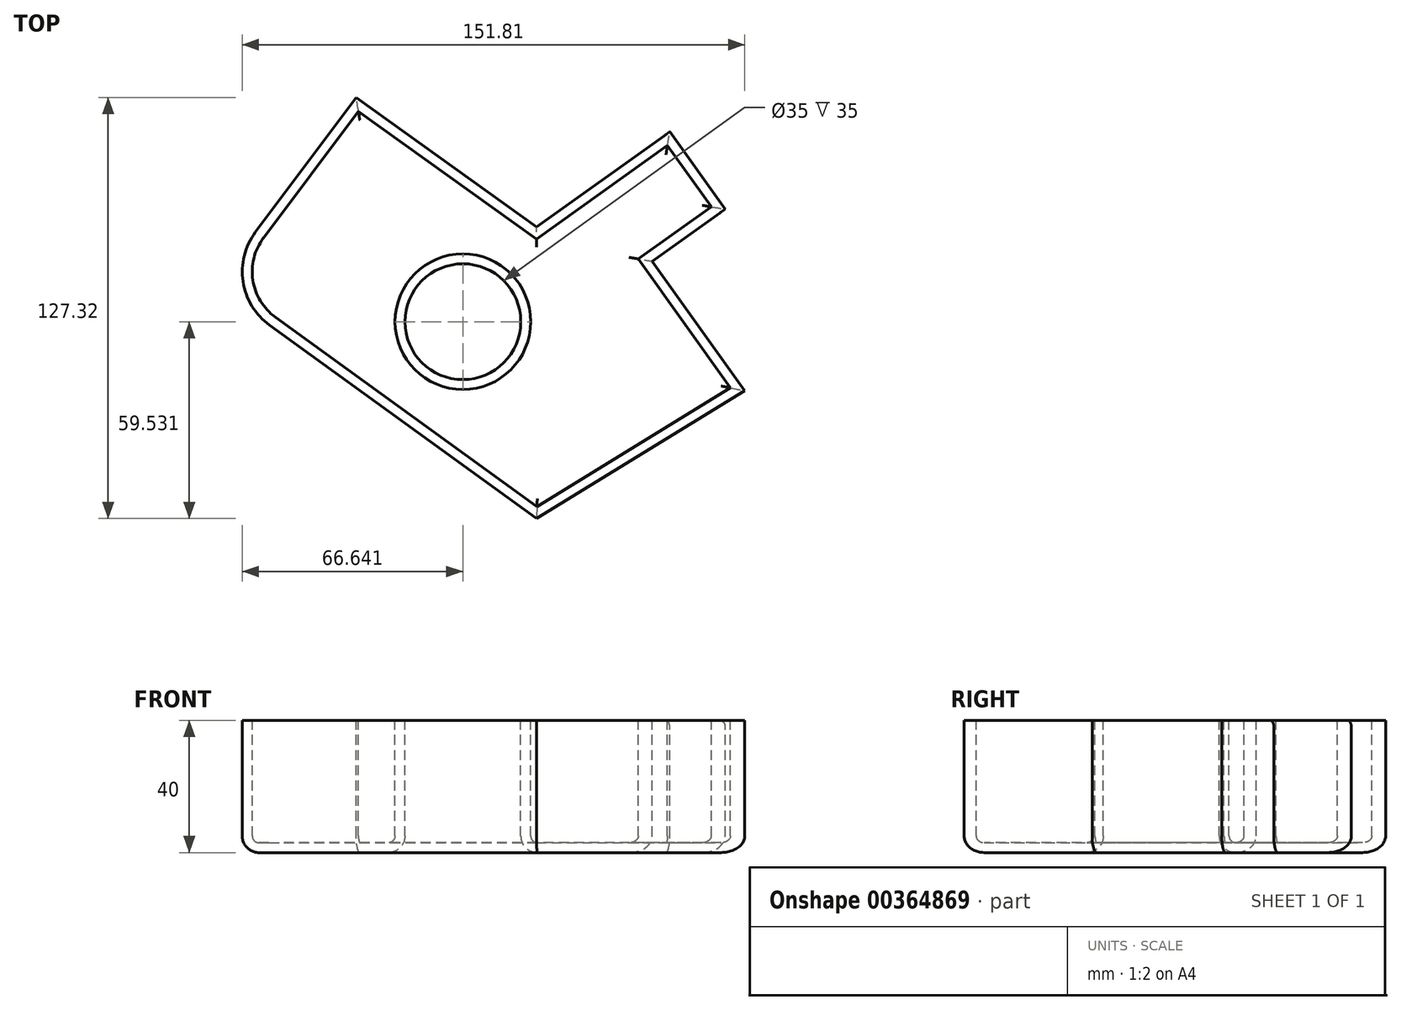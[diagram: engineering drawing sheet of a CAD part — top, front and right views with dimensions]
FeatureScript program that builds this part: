
annotation { "Feature Type Name" : "Feature", "Feature Type Description" : "" }
export const myFeature = defineFeature(function(context is Context, id is Id, definition is map)
    precondition{}
    {
        {
            var Q0;
            Q0=qCreatedBy(makeId("Top.planeOp"),FACE);
            var sketch = newSketch(context, id + "F0", { "sketchPlane" : qUnion([Q0])});
            skLineSegment(sketch, "E0", {"start": v(-82.04, 52.69) * mm, "end": v(-27.6, 13.56) * mm});
            skLineSegment(sketch, "E1", {"start": v(-27.6, 13.56) * mm, "end": v(12.67, 42.32) * mm});
            skLineSegment(sketch, "E2", {"start": v(12.67, 42.32) * mm, "end": v(29.38, 18.93) * mm});
            skLineSegment(sketch, "E3", {"start": v(29.38, 18.93) * mm, "end": v(7.34, 3.19) * mm});
            skLineSegment(sketch, "E4", {"start": v(7.34, 3.19) * mm, "end": v(35.32, -35.99) * mm});
            skLineSegment(sketch, "E5", {"start": v(35.32, -35.99) * mm, "end": v(-27.6, -74.63) * mm});
            skLineSegment(sketch, "E6", {"start": v(-27.6, -74.63) * mm, "end": v(-108.22, -16.2) * mm});
            skLineSegment(sketch, "E7", {"start": v(-112.5, 11.98) * mm, "end": v(-82.04, 52.69) * mm});
            skPoint(sketch, "E8.visualSharp", {"position": v(-124.67, -4.28) * mm});
            skArc(sketch, "E8.filletArc", {"start": v(-112.5, 11.98) * mm, "mid": v(-116.26, -3) * mm, "end": v(-108.22, -16.2) * mm});
            skSolve(sketch);
        }
        {
            var Q0;
            Q0 = qSketchRegion(id + "F0", true);
            extrude(context, id + "F1", {"entities" : qUnion([Q0]), "oppositeDirection" : true, "depth" : 40 * mm});
        }
        {
            var Q0;
            Q0=qCreatedBy(makeId("Top.planeOp"),FACE);
            var sketch = newSketch(context, id + "F2", { "sketchPlane" : qUnion([Q0])});
            skCircle(sketch, "E9", {"center": v(-49.85, -15.1) * mm, "radius": 17.5 * mm});
            skSolve(sketch);
        }
        {
            var Q0;
            Q0 = qSketchRegion(id + "F2", true);
            extrude(context, id + "F3", {"entities" : qUnion([Q0]), "operationType" : NewBodyOperationType.REMOVE, "oppositeDirection" : true, "depth" : 71 * mm, "hasSecondDirection" : true, "secondDirectionOppositeDirection" : false, "secondDirectionDepth" : 36 * mm});
        }
        {
            var Q0;
            Q0=makeQuery(id+"F1.opExtrude","CAP_FACE",FACE,{"disambiguationData":[OSD([sQuery(id+"F0.wireOp",EDGE,"E0"),sQuery(id+"F0.wireOp",EDGE,"E1"),sQuery(id+"F0.wireOp",EDGE,"E2"),sQuery(id+"F0.wireOp",EDGE,"E3"),sQuery(id+"F0.wireOp",EDGE,"E4"),sQuery(id+"F0.wireOp",EDGE,"E5"),sQuery(id+"F0.wireOp",EDGE,"E6"),sQuery(id+"F0.wireOp",EDGE,"E7"),sQuery(id+"F0.wireOp",EDGE,"E8.filletArc")])],"isStart":true});
            shell(context, id + "F4", {"entities" : qUnion([Q0]), "thickness" : 3 * mm});
        }
        {
            var Q0;
            {var subQ0=sQuery(id+"F0.wireOp",EDGE,"E8.filletArc");var subQ1=sQuery(id+"F0.wireOp",EDGE,"E7");var subQ2=sQuery(id+"F0.wireOp",EDGE,"E6");var subQ3=sQuery(id+"F0.wireOp",EDGE,"E5");var subQ4=sQuery(id+"F0.wireOp",EDGE,"E4");var subQ5=sQuery(id+"F0.wireOp",EDGE,"E3");var subQ6=sQuery(id+"F0.wireOp",EDGE,"E2");var subQ7=sQuery(id+"F0.wireOp",EDGE,"E1");var subQ8=sQuery(id+"F0.wireOp",EDGE,"E0");Q0=makeQuery(id+"F4.opShell","OFFSET_FACE",FACE,{"disambiguationData":[OSD([subQ8,subQ7,subQ6,subQ5,subQ4,subQ3,subQ2,subQ1,subQ0]),TDD([makeQuery(id+"F1.opExtrude","CAP_FACE",FACE,{"disambiguationData":[OSD([subQ8,subQ7,subQ6,subQ5,subQ4,subQ3,subQ2,subQ1,subQ0])],"isStart":false})])]});}
            fillet(context, id + "F5", {"entities" : qUnion([Q0]), "radius" : 2 * mm, "tangentPropagation" : true, "allowEdgeOverflow" : false});
        }
        {
            var Q0;
            Q0=makeQuery(id+"F1.opExtrude","CAP_FACE",FACE,{"disambiguationData":[OSD([sQuery(id+"F0.wireOp",EDGE,"E0"),sQuery(id+"F0.wireOp",EDGE,"E1"),sQuery(id+"F0.wireOp",EDGE,"E2"),sQuery(id+"F0.wireOp",EDGE,"E3"),sQuery(id+"F0.wireOp",EDGE,"E4"),sQuery(id+"F0.wireOp",EDGE,"E5"),sQuery(id+"F0.wireOp",EDGE,"E6"),sQuery(id+"F0.wireOp",EDGE,"E7"),sQuery(id+"F0.wireOp",EDGE,"E8.filletArc")])],"isStart":false});
            fillet(context, id + "F6", {"entities" : qUnion([Q0]), "radius" : 5 * mm, "tangentPropagation" : true, "allowEdgeOverflow" : false});
        }
        {
            var Q0;
            Q0=makeQuery(id+"F1.opExtrude","CAP_EDGE",EDGE,{"disambiguationData":[OSD([sQuery(id+"F0.wireOp",EDGE,"E2")])],"isStart":true});
            fillet(context, id + "F7", {"entities" : qUnion([Q0]), "radius" : 2 * mm, "tangentPropagation" : true, "allowEdgeOverflow" : false});
        }
    });
